# Revit family: IS_UltraFlat_K1935_BIM_DE
name_source: partatom
category: Plumbing Fixtures
revit_build: Autodesk Revit MEP 2016 (Build: 20161004_0715(x64)
units: mm (PartAtom-declared; Revit-internal decimal feet)

## family parameters
Always vertical = No
Cut with Voids When Loaded = No
OmniClass Number = 23.45.05.14.17
OmniClass Title = Showers
Part Type = Normal
Room Calculation Point = No
Round Connector Dimension = Use Diameter
Shared = No
Work Plane-Based = No

## types (2) — shared parameters
Accessories = www.idealstandard.de\ersatzteile
AssetType = Fixed
BIMobject category = Shower trays
BOSUseNativeGeometries = 1
Brand = Ideal Standard
Brand url = http://www.idealstandard.de
CodePerformance = DIN EN 14527, DIN EN 249
ConnectionType = Plumbing
CurrencyUnit = €
CurrentRevision = 1
Date of publishing = 42828
DurationUnit = Jaar
EAN code = https://4015413025829
Edition number = 1
ExpectedLife = 25
Features = ULTRA FLAT rectangular shower tray 1000x700mm
HasTray = No
IFC Classification = Sanitary Terminal
IfcExportAs = Sanitary terminal type
IfcExportType = SHOWER
Installation instructions = http://www.idealstandard.de
InstallationInstructions = www.idealstandard.de\produkte
LinearUnits = millimetres
MaintenanceInformation = www.idealstandard.de
Manufacturer = http://www.idealstandard.de
Manufacturer name = Ideal Standard
ManufacturerURL = http://www.idealstandard.de
Material = Sanitary Brass
Material main = Acrylic
NBS Reference Code = 35-06-84
NBS Reference Description = Shower Trays
NettWeight = 18 kg
Nominal height = 47
Nominal width = 700
NominalHeight = 40 mm
NominalLength = 1000 mm
NominalWidth = 700 mm  [stored 2.29659 ft]
Product Guid = 3e7b52bb-c482-4c62-8233-860314d87412
Product SKU = K1935
Product certification = DIN EN 14527, DIN EN 249
Product data url = https://bimobject.com
Product family = ULTRA FLAT
Product group = Shower Tray
Product name = ULTRA FLAT rectangular shower tray 1000x700mm
Product url = http://www.idealstandard.de
ProductInformation = www.idealstandard.de/produkte
QR code = http://bimobject.com
Shape = Rectangular
Size = 1000x700x40 mm
Space = Internal
SpareParts = www.idealstandard.de/ersatzteile
Technical description = http://www.idealstandard.de
URL = http://www.idealstandard.de
Uniclass 2.0 Code = PR-35-06-84
Uniclass 2.0 Description = Shower Trays
Uniclass 2015 Code = Pr_40_20_06_84
Uniclass 2015 Name = Shower trays
Uniclass2015Code = Pr_40_20_06_84
Uniclass2015Title = Shower trays
Uniclass2015Version = Products v1.1
VolumeUnits = Litres
Weight Net (Kg) = 18
zero-valued in all types: Cost

## per-type parameters (varying)
| type | BIMObjectName | BarCode | Color | Finish | MainColor | Model | ModelNumber | Name |
| K193501 ULTRA FLAT rectangular shower tray 1000x700mm | ISI_IdealStandard_ShowerTrays_ULTRAFLAT_K193501 | 4015413025829 | White | White | White | K193501 | K193501 | ISI_IdealStandard_ShowerTrays_ULTRAFLAT_K193501 |
| K1935YK ULTRA FLAT rectangular shower tray 1000x700mm | ISI_IdealStandard_ShowerTrays_ULTRAFLAT_K1935YK | 4015413033121 | White Ideal Grip | White Ideal Grip | White Ideal Grip | K1935YK | K1935YK | ISI_IdealStandard_ShowerTrays_ULTRAFLAT_K1935YK |

note: column(s) folded — value = type name in every type: Description, ModelReference

note: [stored X ft] marks values corroborated as IEEE doubles in the binary element streams (Revit-internal decimal feet)

## geometry (parser evidence)
native form markers: Blend x4, Sweep x1
no freeform markers — native parametric forms only
